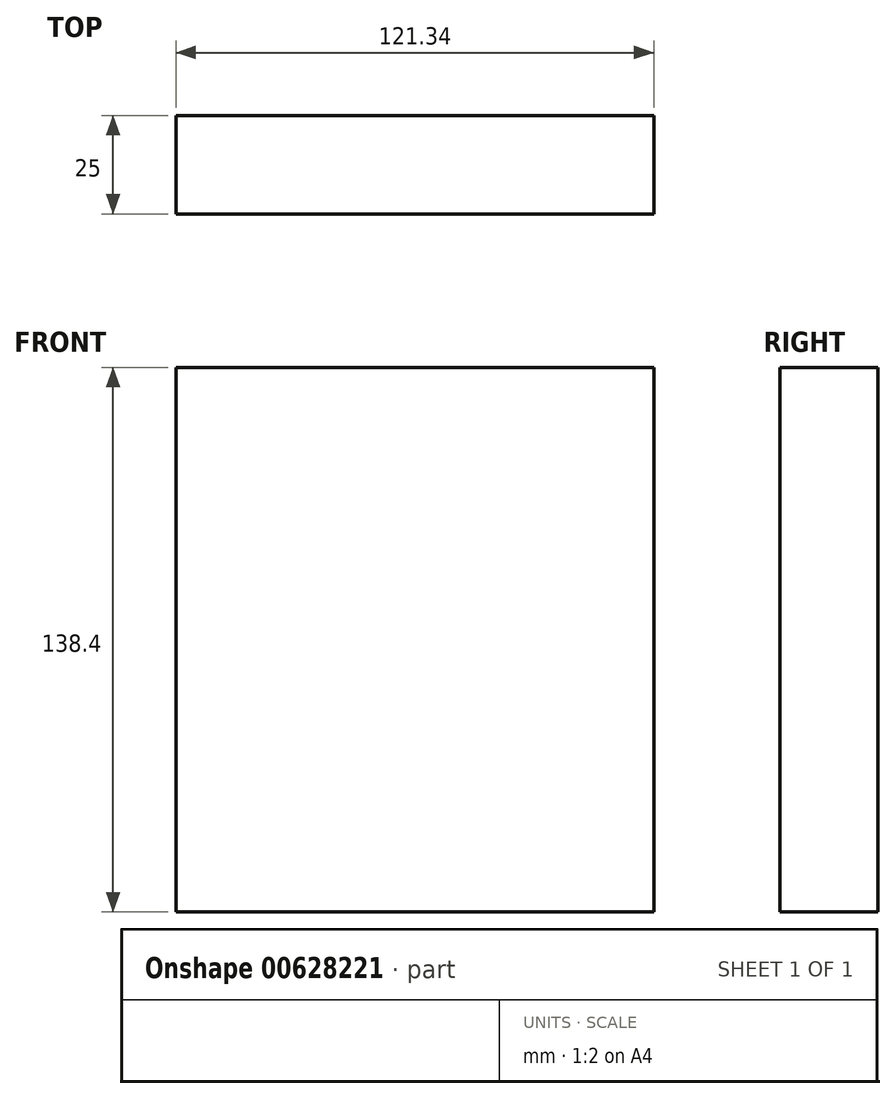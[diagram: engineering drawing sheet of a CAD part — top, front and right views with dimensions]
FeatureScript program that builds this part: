
annotation { "Feature Type Name" : "Feature", "Feature Type Description" : "" }
export const myFeature = defineFeature(function(context is Context, id is Id, definition is map)
    precondition{}
    {
        {
            var Q0;
            Q0=qCreatedBy(makeId("Front.planeOp"),FACE);
            var sketch = newSketch(context, id + "F0", { "sketchPlane" : qUnion([Q0])});
            skLineSegment(sketch, "E0.bottom", {"start": v(60.68, -69.2) * mm, "end": v(-60.68, -69.2) * mm});
            skLineSegment(sketch, "E0.top", {"start": v(60.68, 69.2) * mm, "end": v(-60.68, 69.2) * mm});
            skLineSegment(sketch, "E0.left", {"start": v(60.68, -69.2) * mm, "end": v(60.68, 69.2) * mm});
            skLineSegment(sketch, "E0.right", {"start": v(-60.68, -69.2) * mm, "end": v(-60.68, 69.2) * mm});
            skPoint(sketch, "E0.middle", {"position": v(0, 0) * mm});
            skSolve(sketch);
        }
        {
            var Q0;
            Q0=makeQuery(id+"F0.imprint","IMPRINT",FACE,{"disambiguationData":[TD([[makeQuery(id+"F0.imprint","IMPRINT",EDGE,{"derivedFrom":sQuery(id+"F0.wireOp",EDGE,"E0.bottom")}),-1.0]])]});
            extrude(context, id + "F1", {"entities" : qUnion([Q0]), "depth" : 25 * mm, "offsetDistance" : 25 * mm});
        }
    });
